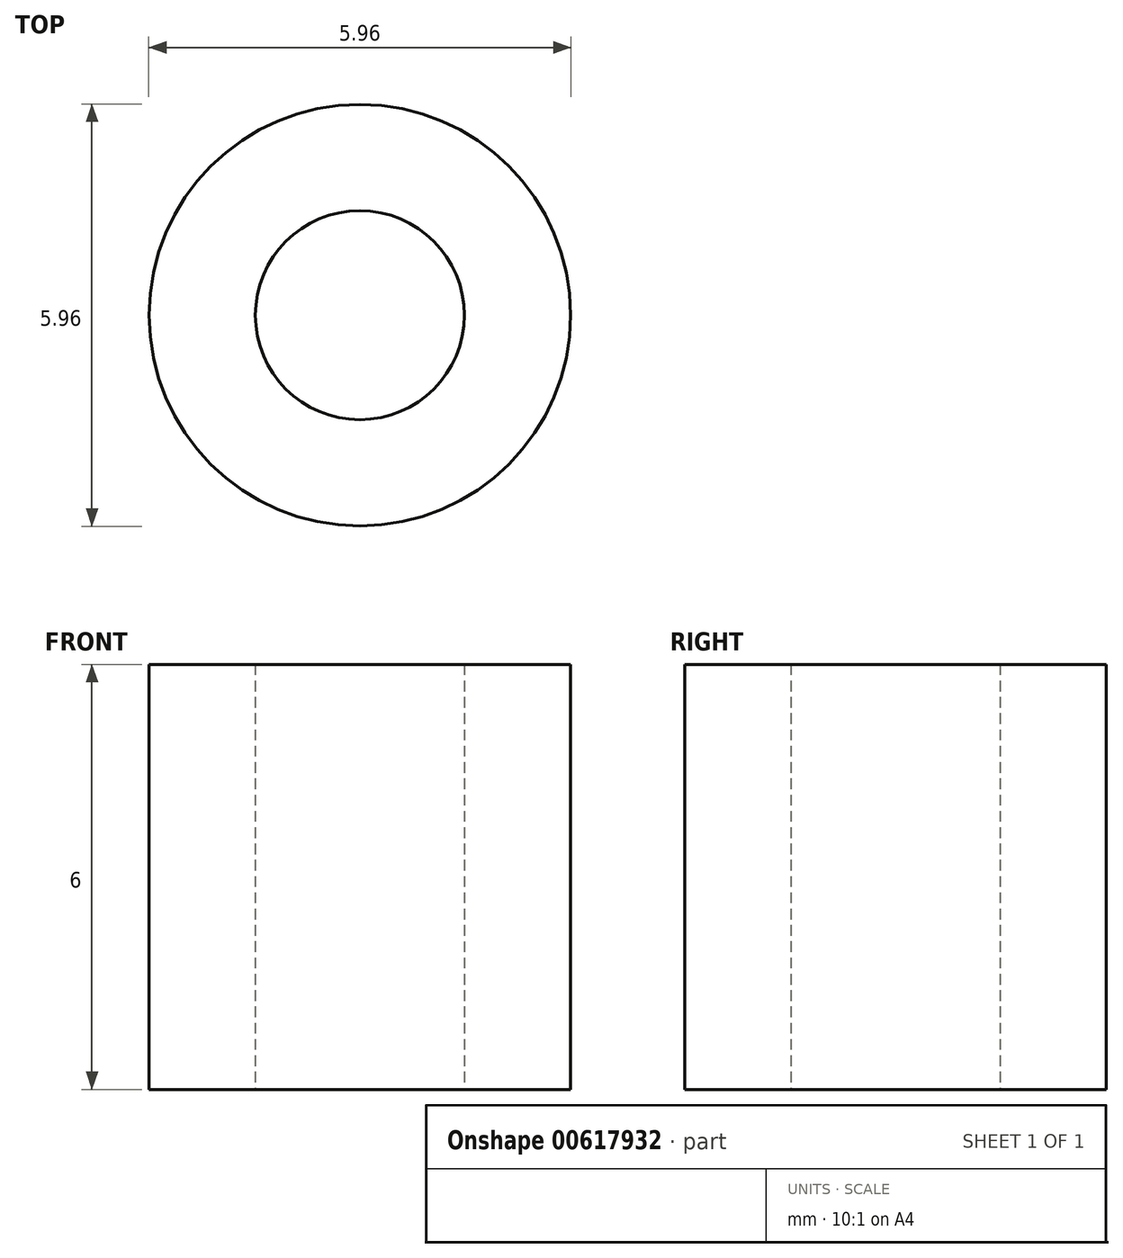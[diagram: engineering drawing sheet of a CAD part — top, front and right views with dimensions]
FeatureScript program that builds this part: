
annotation { "Feature Type Name" : "Feature", "Feature Type Description" : "" }
export const myFeature = defineFeature(function(context is Context, id is Id, definition is map)
    precondition{}
    {
        {
            var Q0;
            Q0=qCreatedBy(makeId("Top.planeOp"),FACE);
            var sketch = newSketch(context, id + "F0", { "sketchPlane" : qUnion([Q0])});
            skCircle(sketch, "E0", {"center": v(0, 0) * mm, "radius": 1.48 * mm});
            skCircle(sketch, "E1", {"center": v(0, 0) * mm, "radius": 2.98 * mm});
            skSolve(sketch);
        }
        {
            var Q0;
            Q0 = qSketchRegion(id + "F0", true);
            extrude(context, id + "F1", {"entities" : qUnion([Q0]), "depth" : 6 * mm, "offsetDistance" : 25 * mm});
        }
    });
